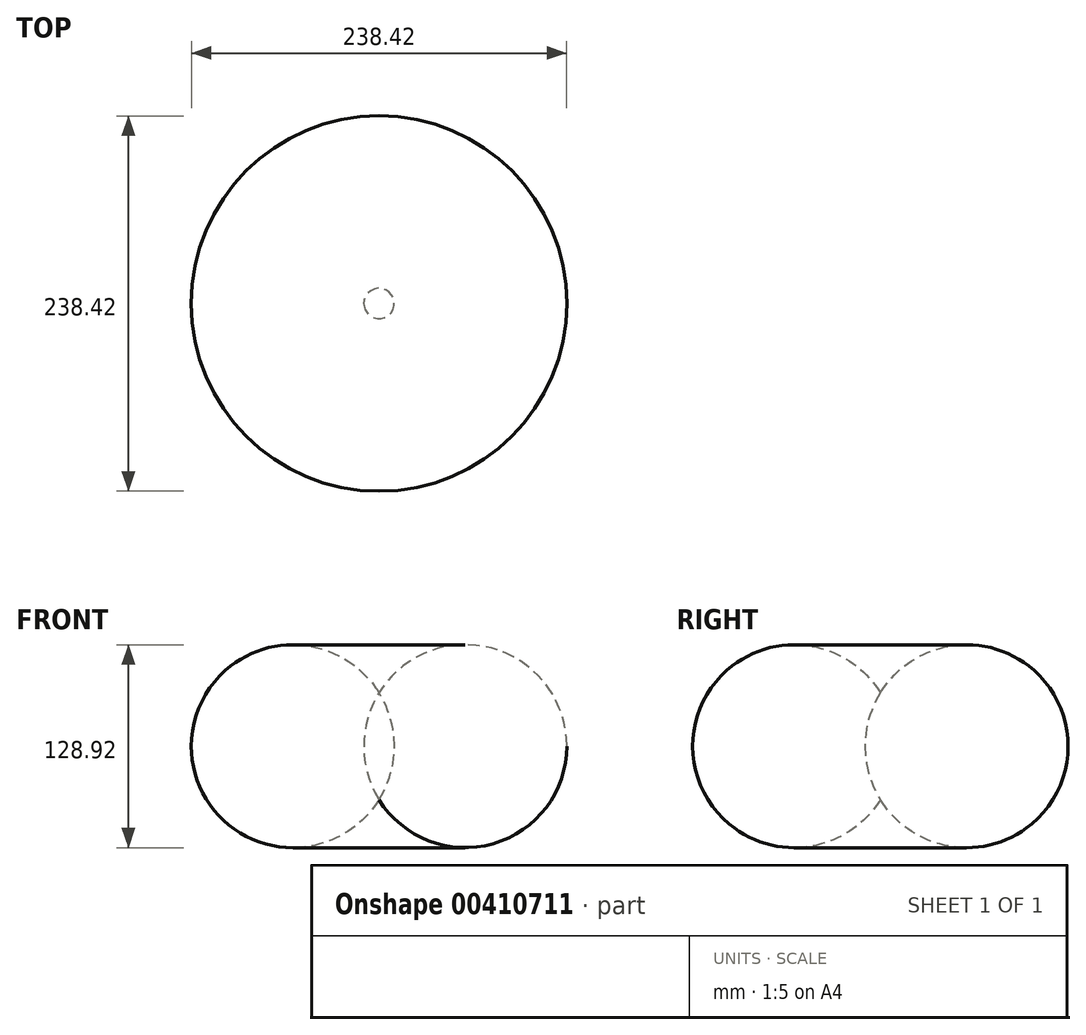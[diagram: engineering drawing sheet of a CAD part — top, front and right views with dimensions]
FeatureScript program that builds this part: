
annotation { "Feature Type Name" : "Feature", "Feature Type Description" : "" }
export const myFeature = defineFeature(function(context is Context, id is Id, definition is map)
    precondition{}
    {
        {
            var Q0;
            Q0=qCreatedBy(makeId("Front.planeOp"),FACE);
            var sketch = newSketch(context, id + "F0", { "sketchPlane" : qUnion([Q0])});
            skLineSegment(sketch, "E0", {"start": v(0, 34.42) * mm, "end": v(0, -33.58) * mm});
            skArc(sketch, "E1", {"start": v(0, -33.58) * mm, "mid": v(119.21, 0.42) * mm, "end": v(0, 34.42) * mm});
            skSolve(sketch);
        }
        {
            var Q0;
            Q0 = qSketchRegion(id + "F0", true);
            var Q1;
            Q1=sQuery(id+"F0.wireOp",EDGE,"E0");
            revolve(context, id + "F1", {"entities" : qUnion([Q0]), "axis" : qUnion([Q1]), "revolveType" : RevolveType.FULL});
        }
    });
